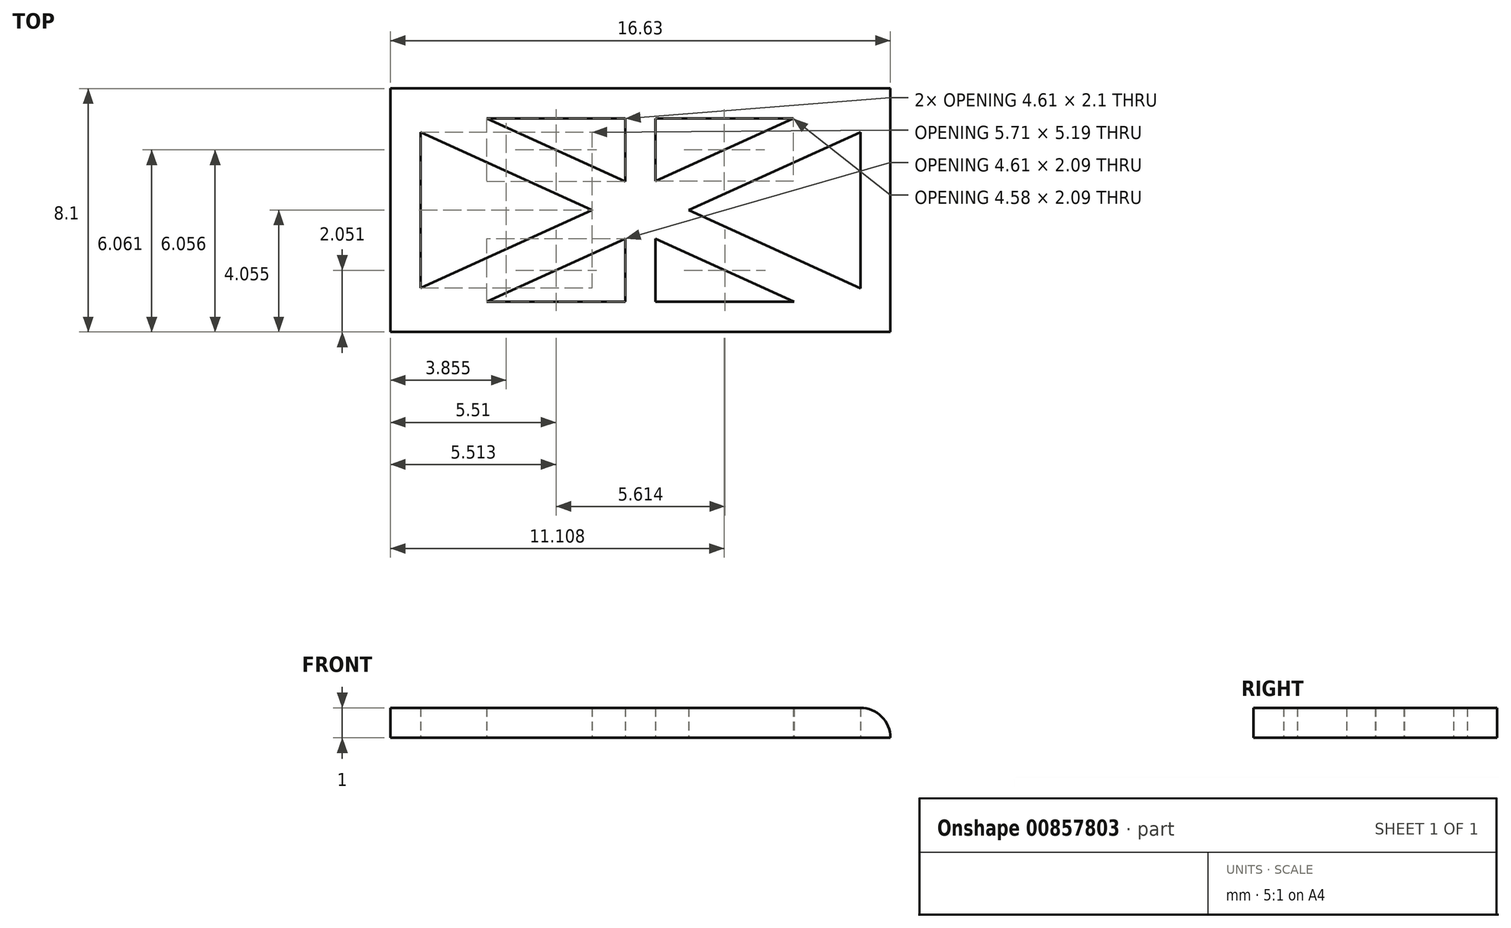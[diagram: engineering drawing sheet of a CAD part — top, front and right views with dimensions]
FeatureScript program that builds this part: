
annotation { "Feature Type Name" : "Feature", "Feature Type Description" : "" }
export const myFeature = defineFeature(function(context is Context, id is Id, definition is map)
    precondition{}
    {
        {
            var Q0;
            Q0=qCreatedBy(makeId("Top.planeOp"),FACE);
            var sketch = newSketch(context, id + "F0", { "sketchPlane" : qUnion([Q0])});
            skLineSegment(sketch, "E0.bottom", {"start": v(-8.3, 3.95) * mm, "end": v(8.32, 3.95) * mm});
            skLineSegment(sketch, "E0.top", {"start": v(-8.3, 2.95) * mm, "end": v(8.32, 2.95) * mm});
            skLineSegment(sketch, "E0.left", {"start": v(-8.3, 3.95) * mm, "end": v(-8.3, 2.95) * mm});
            skLineSegment(sketch, "E0.right", {"start": v(8.32, 3.95) * mm, "end": v(8.32, 2.95) * mm});
            skLineSegment(sketch, "E1.bottom", {"start": v(-8.3, -3.15) * mm, "end": v(8.32, -3.15) * mm});
            skLineSegment(sketch, "E1.top", {"start": v(-8.3, -4.15) * mm, "end": v(8.32, -4.15) * mm});
            skLineSegment(sketch, "E1.left", {"start": v(-8.3, -3.15) * mm, "end": v(-8.3, -4.15) * mm});
            skLineSegment(sketch, "E1.right", {"start": v(8.32, -3.15) * mm, "end": v(8.32, -4.15) * mm});
            skLineSegment(sketch, "E2.bottom", {"start": v(-8.3, 2.95) * mm, "end": v(-7.3, 2.95) * mm});
            skLineSegment(sketch, "E2.top", {"start": v(-8.3, -3.15) * mm, "end": v(-7.3, -3.15) * mm});
            skLineSegment(sketch, "E2.left", {"start": v(-8.3, 2.95) * mm, "end": v(-8.3, -3.15) * mm});
            skLineSegment(sketch, "E2.right", {"start": v(-7.3, 2.95) * mm, "end": v(-7.3, -3.15) * mm});
            skLineSegment(sketch, "E3.bottom", {"start": v(8.32, 2.95) * mm, "end": v(7.32, 2.95) * mm});
            skLineSegment(sketch, "E3.top", {"start": v(8.32, -3.15) * mm, "end": v(7.32, -3.15) * mm});
            skLineSegment(sketch, "E3.left", {"start": v(8.32, 2.95) * mm, "end": v(8.32, -3.15) * mm});
            skLineSegment(sketch, "E3.right", {"start": v(7.32, 2.95) * mm, "end": v(7.32, -3.15) * mm});
            skLineSegment(sketch, "E4", {"start": v(0.5, 2.95) * mm, "end": v(0.5, -3.15) * mm});
            skLineSegment(sketch, "E5", {"start": v(-0.5, 2.95) * mm, "end": v(-0.5, -3.15) * mm});
            skLineSegment(sketch, "E6", {"start": v(-8.3, -3.15) * mm, "end": v(7.29, 3.95) * mm});
            skLineSegment(sketch, "E7", {"start": v(-7.3, -4.15) * mm, "end": v(8.32, 2.95) * mm});
            skLineSegment(sketch, "E8", {"start": v(-8.3, 2.95) * mm, "end": v(7.32, -4.15) * mm});
            skLineSegment(sketch, "E9", {"start": v(8.32, -3.15) * mm, "end": v(-7.3, 3.95) * mm});
            skSolve(sketch);
        }
        {
            var Q0;
            {var subQ0=sQuery(id+"F0.wireOp",EDGE,"E2.left");Q0=makeQuery(id+"F0.imprint","IMPRINT",FACE,{"disambiguationData":[TD([[makeQuery(id+"F0.imprint","IMPRINT",EDGE,{"derivedFrom":subQ0}),1.0]])]});}
            var Q1;
            {var subQ0=sQuery(id+"F0.wireOp",EDGE,"E2.right");var subQ1=sQuery(id+"F0.wireOp",EDGE,"E0.top");var subQ2=makeQuery(id+"F0.imprint","INTERSECT",VERTEX,{"derivedFrom":[subQ1,subQ0]});Q1=makeQuery(id+"F0.imprint","IMPRINT",FACE,{"disambiguationData":[TD([[makeQuery(id+"F0.imprint","IMPRINT",EDGE,{"disambiguationData":[TD([[subQ2,-1.0]])],"derivedFrom":subQ0}),-1.0]])]});}
            var Q2;
            {var subQ0=sQuery(id+"F0.wireOp",EDGE,"E0.left");Q2=makeQuery(id+"F0.imprint","IMPRINT",FACE,{"disambiguationData":[TD([[makeQuery(id+"F0.imprint","IMPRINT",EDGE,{"derivedFrom":subQ0}),1.0]])]});}
            var Q3;
            {var subQ0=sQuery(id+"F0.wireOp",EDGE,"E2.right");var subQ1=sQuery(id+"F0.wireOp",EDGE,"E1.bottom");var subQ2=makeQuery(id+"F0.imprint","INTERSECT",VERTEX,{"derivedFrom":[subQ1,subQ0]});Q3=makeQuery(id+"F0.imprint","IMPRINT",FACE,{"disambiguationData":[TD([[makeQuery(id+"F0.imprint","IMPRINT",EDGE,{"disambiguationData":[TD([[subQ2,1.0]])],"derivedFrom":subQ0}),-1.0]])]});}
            var Q4;
            {var subQ0=sQuery(id+"F0.wireOp",EDGE,"E1.left");Q4=makeQuery(id+"F0.imprint","IMPRINT",FACE,{"disambiguationData":[TD([[makeQuery(id+"F0.imprint","IMPRINT",EDGE,{"derivedFrom":subQ0}),1.0]])]});}
            var Q5;
            {var subQ5=sQuery(id+"F0.wireOp",EDGE,"E1.bottom");var subQ6=makeQuery(id+"F0.imprint","INTERSECT",VERTEX,{"derivedFrom":[subQ5,sQuery(id+"F0.wireOp",EDGE,"E4")]});Q5=makeQuery(id+"F0.imprint","IMPRINT",FACE,{"disambiguationData":[TD([[makeQuery(id+"F0.imprint","IMPRINT",EDGE,{"disambiguationData":[TD([[subQ6,-1.0]])],"derivedFrom":subQ5}),-1.0]])]});}
            var Q6;
            {var subQ1=sQuery(id+"F0.wireOp",EDGE,"E2.right");var subQ9=sQuery(id+"F0.wireOp",EDGE,"E1.bottom");var subQ10=makeQuery(id+"F0.imprint","INTERSECT",VERTEX,{"derivedFrom":[subQ9,subQ1]});Q6=makeQuery(id+"F0.imprint","IMPRINT",FACE,{"disambiguationData":[TD([[makeQuery(id+"F0.imprint","IMPRINT",EDGE,{"disambiguationData":[TD([[subQ10,-1.0]])],"derivedFrom":subQ9}),1.0]])]});}
            var Q7;
            {var subQ0=sQuery(id+"F0.wireOp",EDGE,"E7");var subQ1=sQuery(id+"F0.wireOp",EDGE,"E4");var subQ2=makeQuery(id+"F0.imprint","INTERSECT",VERTEX,{"derivedFrom":[subQ1,subQ0]});Q7=makeQuery(id+"F0.imprint","IMPRINT",FACE,{"disambiguationData":[TD([[makeQuery(id+"F0.imprint","IMPRINT",EDGE,{"disambiguationData":[TD([[subQ2,1.0]])],"derivedFrom":subQ1}),-1.0]])]});}
            var Q8;
            {var subQ0=sQuery(id+"F0.wireOp",EDGE,"E7");var subQ1=sQuery(id+"F0.wireOp",EDGE,"E5");var subQ2=makeQuery(id+"F0.imprint","INTERSECT",VERTEX,{"derivedFrom":[subQ1,subQ0]});Q8=makeQuery(id+"F0.imprint","IMPRINT",FACE,{"disambiguationData":[TD([[makeQuery(id+"F0.imprint","IMPRINT",EDGE,{"disambiguationData":[TD([[subQ2,1.0]])],"derivedFrom":subQ1}),1.0]])]});}
            var Q9;
            {var subQ0=sQuery(id+"F0.wireOp",EDGE,"E8");var subQ1=sQuery(id+"F0.wireOp",EDGE,"E4");var subQ2=makeQuery(id+"F0.imprint","INTERSECT",VERTEX,{"derivedFrom":[subQ1,subQ0]});Q9=makeQuery(id+"F0.imprint","IMPRINT",FACE,{"disambiguationData":[TD([[makeQuery(id+"F0.imprint","IMPRINT",EDGE,{"disambiguationData":[TD([[subQ2,1.0]])],"derivedFrom":subQ1}),-1.0]])]});}
            var Q10;
            {var subQ0=sQuery(id+"F0.wireOp",EDGE,"E7");var subQ1=sQuery(id+"F0.wireOp",EDGE,"E4");var subQ2=makeQuery(id+"F0.imprint","INTERSECT",VERTEX,{"derivedFrom":[subQ1,subQ0]});Q10=makeQuery(id+"F0.imprint","IMPRINT",FACE,{"disambiguationData":[TD([[makeQuery(id+"F0.imprint","IMPRINT",EDGE,{"disambiguationData":[TD([[subQ2,1.0]])],"derivedFrom":subQ1}),1.0]])]});}
            var Q11;
            {var subQ0=sQuery(id+"F0.wireOp",EDGE,"E6");var subQ1=sQuery(id+"F0.wireOp",EDGE,"E5");var subQ2=makeQuery(id+"F0.imprint","INTERSECT",VERTEX,{"derivedFrom":[subQ1,subQ0]});Q11=makeQuery(id+"F0.imprint","IMPRINT",FACE,{"disambiguationData":[TD([[makeQuery(id+"F0.imprint","IMPRINT",EDGE,{"disambiguationData":[TD([[subQ2,1.0]])],"derivedFrom":subQ1}),1.0]])]});}
            var Q12;
            {var subQ0=sQuery(id+"F0.wireOp",EDGE,"E6");var subQ1=sQuery(id+"F0.wireOp",EDGE,"E4");var subQ2=makeQuery(id+"F0.imprint","INTERSECT",VERTEX,{"derivedFrom":[subQ1,subQ0]});Q12=makeQuery(id+"F0.imprint","IMPRINT",FACE,{"disambiguationData":[TD([[makeQuery(id+"F0.imprint","IMPRINT",EDGE,{"disambiguationData":[TD([[subQ2,-1.0]])],"derivedFrom":subQ1}),-1.0]])]});}
            var Q13;
            {var subQ1=sQuery(id+"F0.wireOp",EDGE,"E0.top");var subQ7=sQuery(id+"F0.wireOp",EDGE,"E5");var subQ9=makeQuery(id+"F0.imprint","INTERSECT",VERTEX,{"derivedFrom":[subQ1,subQ7]});Q13=makeQuery(id+"F0.imprint","IMPRINT",FACE,{"disambiguationData":[TD([[makeQuery(id+"F0.imprint","IMPRINT",EDGE,{"disambiguationData":[TD([[subQ9,-1.0]])],"derivedFrom":subQ1}),-1.0]])]});}
            var Q14;
            {var subQ5=sQuery(id+"F0.wireOp",EDGE,"E4");var subQ6=sQuery(id+"F0.wireOp",EDGE,"E1.bottom");var subQ7=makeQuery(id+"F0.imprint","INTERSECT",VERTEX,{"derivedFrom":[subQ6,subQ5]});Q14=makeQuery(id+"F0.imprint","IMPRINT",FACE,{"disambiguationData":[TD([[makeQuery(id+"F0.imprint","IMPRINT",EDGE,{"disambiguationData":[TD([[subQ7,1.0]])],"derivedFrom":subQ6}),1.0]])]});}
            var Q15;
            {var subQ1=sQuery(id+"F0.wireOp",EDGE,"E0.top");var subQ8=sQuery(id+"F0.wireOp",EDGE,"E3.right");var subQ10=makeQuery(id+"F0.imprint","INTERSECT",VERTEX,{"derivedFrom":[subQ1,subQ8]});Q15=makeQuery(id+"F0.imprint","IMPRINT",FACE,{"disambiguationData":[TD([[makeQuery(id+"F0.imprint","IMPRINT",EDGE,{"disambiguationData":[TD([[subQ10,1.0]])],"derivedFrom":subQ1}),-1.0]])]});}
            var Q16;
            {var subQ0=sQuery(id+"F0.wireOp",EDGE,"E0.right");Q16=makeQuery(id+"F0.imprint","IMPRINT",FACE,{"disambiguationData":[TD([[makeQuery(id+"F0.imprint","IMPRINT",EDGE,{"derivedFrom":subQ0}),-1.0]])]});}
            var Q17;
            {var subQ0=sQuery(id+"F0.wireOp",EDGE,"E7");var subQ3=sQuery(id+"F0.wireOp",EDGE,"E3.right");var subQ5=makeQuery(id+"F0.imprint","INTERSECT",VERTEX,{"derivedFrom":[subQ3,subQ0]});Q17=makeQuery(id+"F0.imprint","IMPRINT",FACE,{"disambiguationData":[TD([[makeQuery(id+"F0.imprint","IMPRINT",EDGE,{"disambiguationData":[TD([[subQ5,1.0]])],"derivedFrom":subQ3}),1.0]])]});}
            var Q18;
            {var subQ0=sQuery(id+"F0.wireOp",EDGE,"E3.left");Q18=makeQuery(id+"F0.imprint","IMPRINT",FACE,{"disambiguationData":[TD([[makeQuery(id+"F0.imprint","IMPRINT",EDGE,{"derivedFrom":subQ0}),-1.0]])]});}
            var Q19;
            {var subQ1=sQuery(id+"F0.wireOp",EDGE,"E1.bottom");var subQ3=sQuery(id+"F0.wireOp",EDGE,"E3.right");var subQ4=makeQuery(id+"F0.imprint","INTERSECT",VERTEX,{"derivedFrom":[subQ1,subQ3]});Q19=makeQuery(id+"F0.imprint","IMPRINT",FACE,{"disambiguationData":[TD([[makeQuery(id+"F0.imprint","IMPRINT",EDGE,{"disambiguationData":[TD([[subQ4,1.0]])],"derivedFrom":subQ3}),1.0]])]});}
            var Q20;
            {var subQ0=sQuery(id+"F0.wireOp",EDGE,"E1.right");Q20=makeQuery(id+"F0.imprint","IMPRINT",FACE,{"disambiguationData":[TD([[makeQuery(id+"F0.imprint","IMPRINT",EDGE,{"derivedFrom":subQ0}),-1.0]])]});}
            var Q21;
            {var subQ7=sQuery(id+"F0.wireOp",EDGE,"E0.top");var subQ9=sQuery(id+"F0.wireOp",EDGE,"E9");var subQ11=makeQuery(id+"F0.imprint","INTERSECT",VERTEX,{"derivedFrom":[subQ7,subQ9]});Q21=makeQuery(id+"F0.imprint","IMPRINT",FACE,{"disambiguationData":[TD([[makeQuery(id+"F0.imprint","IMPRINT",EDGE,{"disambiguationData":[TD([[subQ11,1.0]])],"derivedFrom":subQ7}),-1.0]])]});}
            var Q22;
            {var subQ0=sQuery(id+"F0.wireOp",EDGE,"E6");var subQ1=sQuery(id+"F0.wireOp",EDGE,"E5");var subQ2=makeQuery(id+"F0.imprint","INTERSECT",VERTEX,{"derivedFrom":[subQ1,subQ0]});Q22=makeQuery(id+"F0.imprint","IMPRINT",FACE,{"disambiguationData":[TD([[makeQuery(id+"F0.imprint","IMPRINT",EDGE,{"disambiguationData":[TD([[subQ2,-1.0]])],"derivedFrom":subQ1}),-1.0]])]});}
            var Q23;
            {var subQ5=sQuery(id+"F0.wireOp",EDGE,"E3.right");var subQ9=sQuery(id+"F0.wireOp",EDGE,"E1.bottom");var subQ10=makeQuery(id+"F0.imprint","INTERSECT",VERTEX,{"derivedFrom":[subQ9,subQ5]});Q23=makeQuery(id+"F0.imprint","IMPRINT",FACE,{"disambiguationData":[TD([[makeQuery(id+"F0.imprint","IMPRINT",EDGE,{"disambiguationData":[TD([[subQ10,1.0]])],"derivedFrom":subQ9}),1.0]])]});}
            var Q24;
            {var subQ5=sQuery(id+"F0.wireOp",EDGE,"E9");var subQ7=sQuery(id+"F0.wireOp",EDGE,"E0.bottom");var subQ8=makeQuery(id+"F0.imprint","INTERSECT",VERTEX,{"derivedFrom":[subQ7,subQ5]});Q24=makeQuery(id+"F0.imprint","IMPRINT",FACE,{"disambiguationData":[TD([[makeQuery(id+"F0.imprint","IMPRINT",EDGE,{"disambiguationData":[TD([[subQ8,-1.0]])],"derivedFrom":subQ7}),-1.0]])]});}
            extrude(context, id + "F1", {"entities" : qUnion([Q0, Q1, Q2, Q3, Q4, Q5, Q6, Q7, Q8, Q9, Q10, Q11, Q12, Q13, Q14, Q15, Q16, Q17, Q18, Q19, Q20, Q21, Q22, Q23, Q24]), "depth" : 1 * mm, "offsetDistance" : 25 * mm});
        }
        {
            var Q0;
            Q0=makeQuery(id+"F1.opExtrude","CAP_EDGE",EDGE,{"disambiguationData":[OSD([sQuery(id+"F0.wireOp",EDGE,"E0.right"),sQuery(id+"F0.wireOp",EDGE,"E1.right"),sQuery(id+"F0.wireOp",EDGE,"E3.left")])],"isStart":false});
            fillet(context, id + "F2", {"entities" : qUnion([Q0]), "radius" : 1 * mm, "tangentPropagation" : true, "allowEdgeOverflow" : false});
        }
    });
